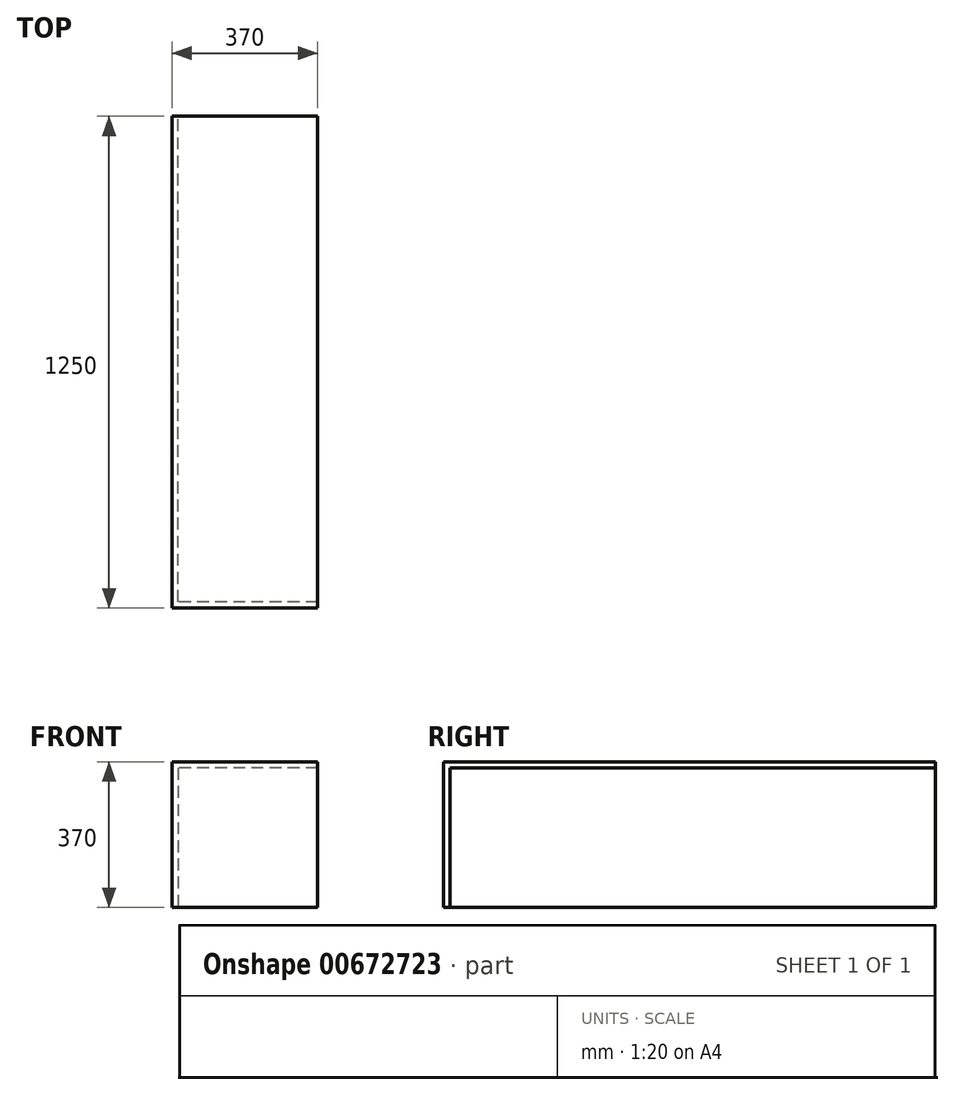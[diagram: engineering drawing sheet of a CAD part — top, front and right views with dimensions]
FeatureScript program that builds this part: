
annotation { "Feature Type Name" : "Feature", "Feature Type Description" : "" }
export const myFeature = defineFeature(function(context is Context, id is Id, definition is map)
    precondition{}
    {
        {
            var Q0;
            Q0=qCreatedBy(makeId("Top.planeOp"),FACE);
            var sketch = newSketch(context, id + "F0", { "sketchPlane" : qUnion([Q0])});
            skLineSegment(sketch, "E0.bottom", {"start": v(0, 0) * mm, "end": v(-370, 0) * mm});
            skLineSegment(sketch, "E0.top", {"start": v(0, 1250) * mm, "end": v(-370, 1250) * mm});
            skLineSegment(sketch, "E0.left", {"start": v(0, 0) * mm, "end": v(0, 1250) * mm});
            skLineSegment(sketch, "E0.right", {"start": v(-370, 0) * mm, "end": v(-370, 1250) * mm});
            skSolve(sketch);
        }
        {
            var Q0;
            Q0=makeQuery(id+"F0.imprint","IMPRINT",FACE,{"disambiguationData":[TD([[makeQuery(id+"F0.imprint","IMPRINT",EDGE,{"derivedFrom":sQuery(id+"F0.wireOp",EDGE,"E0.bottom")}),-1.0]])]});
            extrude(context, id + "F1", {"entities" : qUnion([Q0]), "depth" : 370 * mm, "offsetDistance" : 25 * mm});
        }
        {
            var Q0;
            Q0=makeQuery(id+"F1.opExtrude","SWEPT_FACE",FACE,{"disambiguationData":[OSD([sQuery(id+"F0.wireOp",EDGE,"E0.left")])]});
            var Q1;
            Q1=makeQuery(id+"F1.opExtrude","CAP_FACE",FACE,{"disambiguationData":[OSD([sQuery(id+"F0.wireOp",EDGE,"E0.bottom"),sQuery(id+"F0.wireOp",EDGE,"E0.top"),sQuery(id+"F0.wireOp",EDGE,"E0.left"),sQuery(id+"F0.wireOp",EDGE,"E0.right")])],"isStart":true});
            var Q2;
            Q2=makeQuery(id+"F1.opExtrude","SWEPT_FACE",FACE,{"disambiguationData":[OSD([sQuery(id+"F0.wireOp",EDGE,"E0.top")])]});
            shell(context, id + "F2", {"entities" : qUnion([Q0, Q1, Q2]), "thickness" : 16 * mm});
        }
    });
